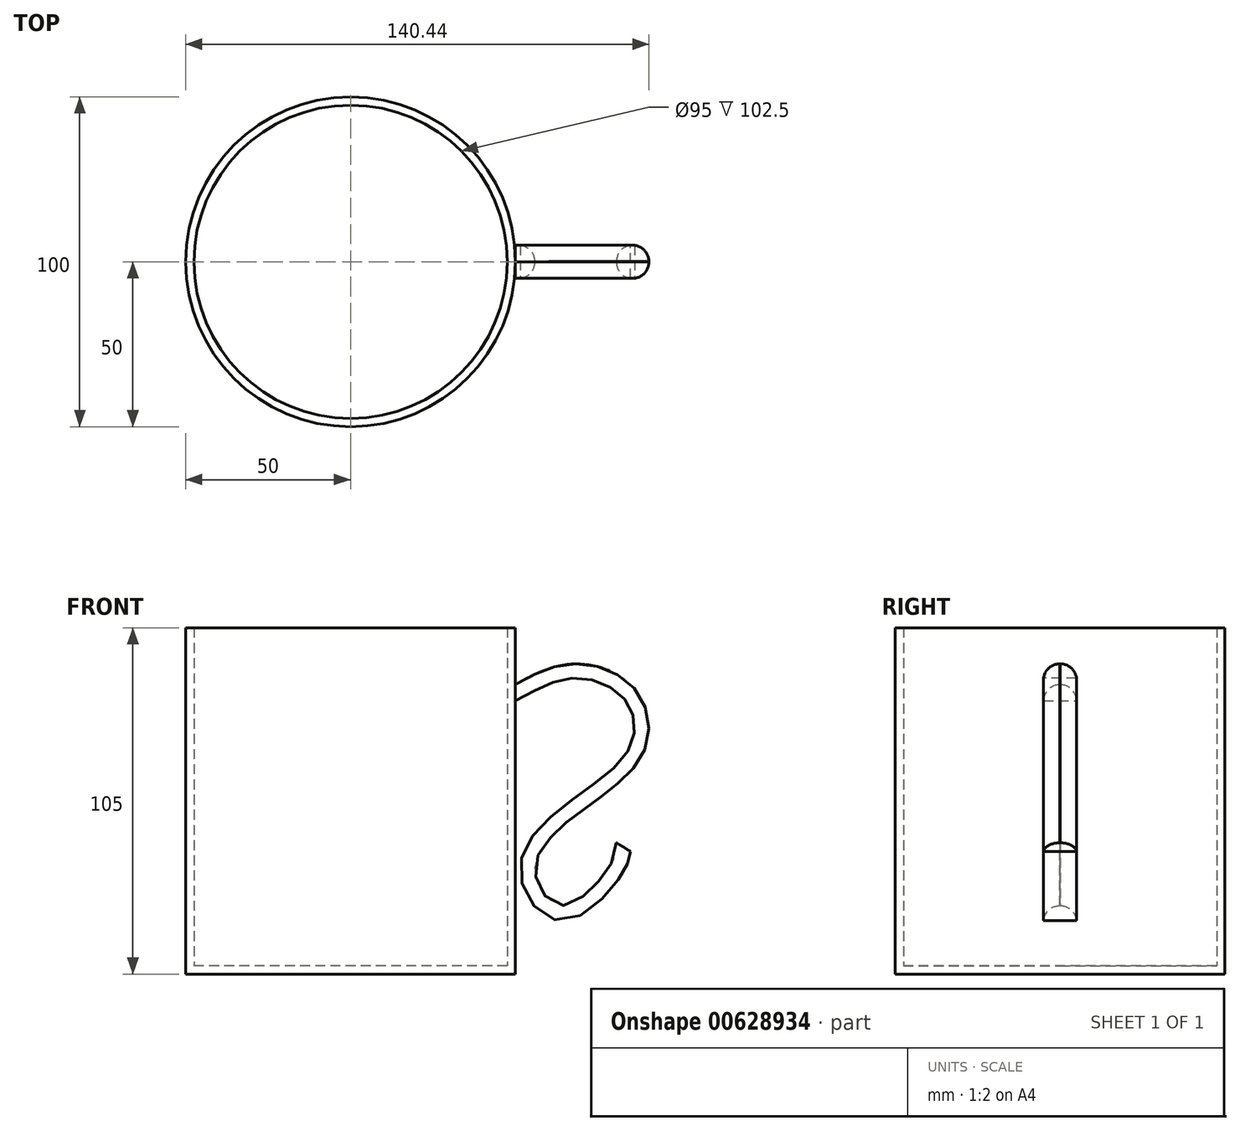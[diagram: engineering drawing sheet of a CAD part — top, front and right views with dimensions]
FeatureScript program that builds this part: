
annotation { "Feature Type Name" : "Feature", "Feature Type Description" : "" }
export const myFeature = defineFeature(function(context is Context, id is Id, definition is map)
    precondition{}
    {
        {
            var Q0;
            Q0=qCreatedBy(makeId("Top.planeOp"),FACE);
            var sketch = newSketch(context, id + "F0", { "sketchPlane" : qUnion([Q0])});
            skCircle(sketch, "E0", {"center": v(0, 0) * mm, "radius": 50 * mm});
            skSolve(sketch);
        }
        {
            var Q0;
            Q0 = qSketchRegion(id + "F0", true);
            extrude(context, id + "F1", {"entities" : qUnion([Q0]), "depth" : 105 * mm, "offsetDistance" : 25 * mm});
        }
        {
            var Q0;
            Q0=qCreatedBy(makeId("Front.planeOp"),FACE);
            var sketch = newSketch(context, id + "F2", { "sketchPlane" : qUnion([Q0])});
            skFitSpline(sketch, "E1", {"points": [v(50.69, 85.39) * mm, v(68.43, 91.56) * mm, v(85.02, 83.84) * mm, v(86.18, 67.64) * mm, v(66.89, 50.28) * mm, v(53.39, 31.77) * mm, v(63.8, 18.27) * mm, v(81.16, 32.15) * mm, v(83.09, 39.1) * mm], "startDerivative": vector(134.74, 72.2) * mm, "endDerivative": vector(4.44, 74.08) * mm});
            skSolve(sketch);
        }
        {
            var Q0;
            Q0=qCreatedBy(makeId("Right.planeOp"),FACE);
            cPlane(context, id + "F3", {"entities" : qUnion([Q0]), "cplaneType" : CPlaneType.OFFSET, "offset" : 50 * mm, "width" : 150 * mm, "height" : 150 * mm});
        }
        {
            var Q0;
            Q0=qCreatedBy(id+"F3.planeOp",FACE);
            var sketch = newSketch(context, id + "F4", { "sketchPlane" : qUnion([Q0])});
            skLineSegment(sketch, "E2.bottom", {"start": v(-5, 87.89) * mm, "end": v(5, 87.89) * mm});
            skLineSegment(sketch, "E2.top", {"start": v(-5, 82.89) * mm, "end": v(5, 82.89) * mm});
            skLineSegment(sketch, "E2.left", {"start": v(-5, 87.89) * mm, "end": v(-5, 82.89) * mm});
            skLineSegment(sketch, "E2.right", {"start": v(5, 87.89) * mm, "end": v(5, 82.89) * mm});
            skPoint(sketch, "E2.middle", {"position": v(0, 85.39) * mm});
            skSolve(sketch);
        }
        {
            var Q0;
            Q0 = qSketchRegion(id + "F4", true);
            var Q1;
            Q1=sQuery(id+"F2.wireOp",EDGE,"E1");
            sweep(context, id + "F5", {"operationType" : NewBodyOperationType.ADD, "profiles" : qUnion([Q0]), "path" : qUnion([Q1])});
        }
        {
            var Q0;
            Q0=makeQuery(id+"F1.opExtrude","CAP_FACE",FACE,{"disambiguationData":[OSD([sQuery(id+"F0.wireOp",EDGE,"E0")])],"isStart":false});
            shell(context, id + "F6", {"entities" : qUnion([Q0]), "thickness" : 2.5 * mm});
        }
        {
            var Q0;
            Q0=makeQuery(id+"F5.opSweep","SWEPT_EDGE",EDGE,{"disambiguationData":[OSD([sQuery(id+"F2.wireOp",EDGE,"E1"),sQuery(id+"F4.wireOp",EDGE,"E2.bottom"),sQuery(id+"F4.wireOp",EDGE,"E2.right")])]});
            fillet(context, id + "F7", {"entities" : qUnion([Q0]), "radius" : 5 * mm, "tangentPropagation" : true, "allowEdgeOverflow" : false});
        }
        {
            var Q0;
            Q0=makeQuery(id+"F5.opSweep","SWEPT_EDGE",EDGE,{"disambiguationData":[OSD([sQuery(id+"F2.wireOp",EDGE,"E1"),sQuery(id+"F4.wireOp",EDGE,"E2.bottom"),sQuery(id+"F4.wireOp",EDGE,"E2.left")])]});
            fillet(context, id + "F8", {"entities" : qUnion([Q0]), "radius" : 5 * mm, "tangentPropagation" : true, "allowEdgeOverflow" : false});
        }
    });
